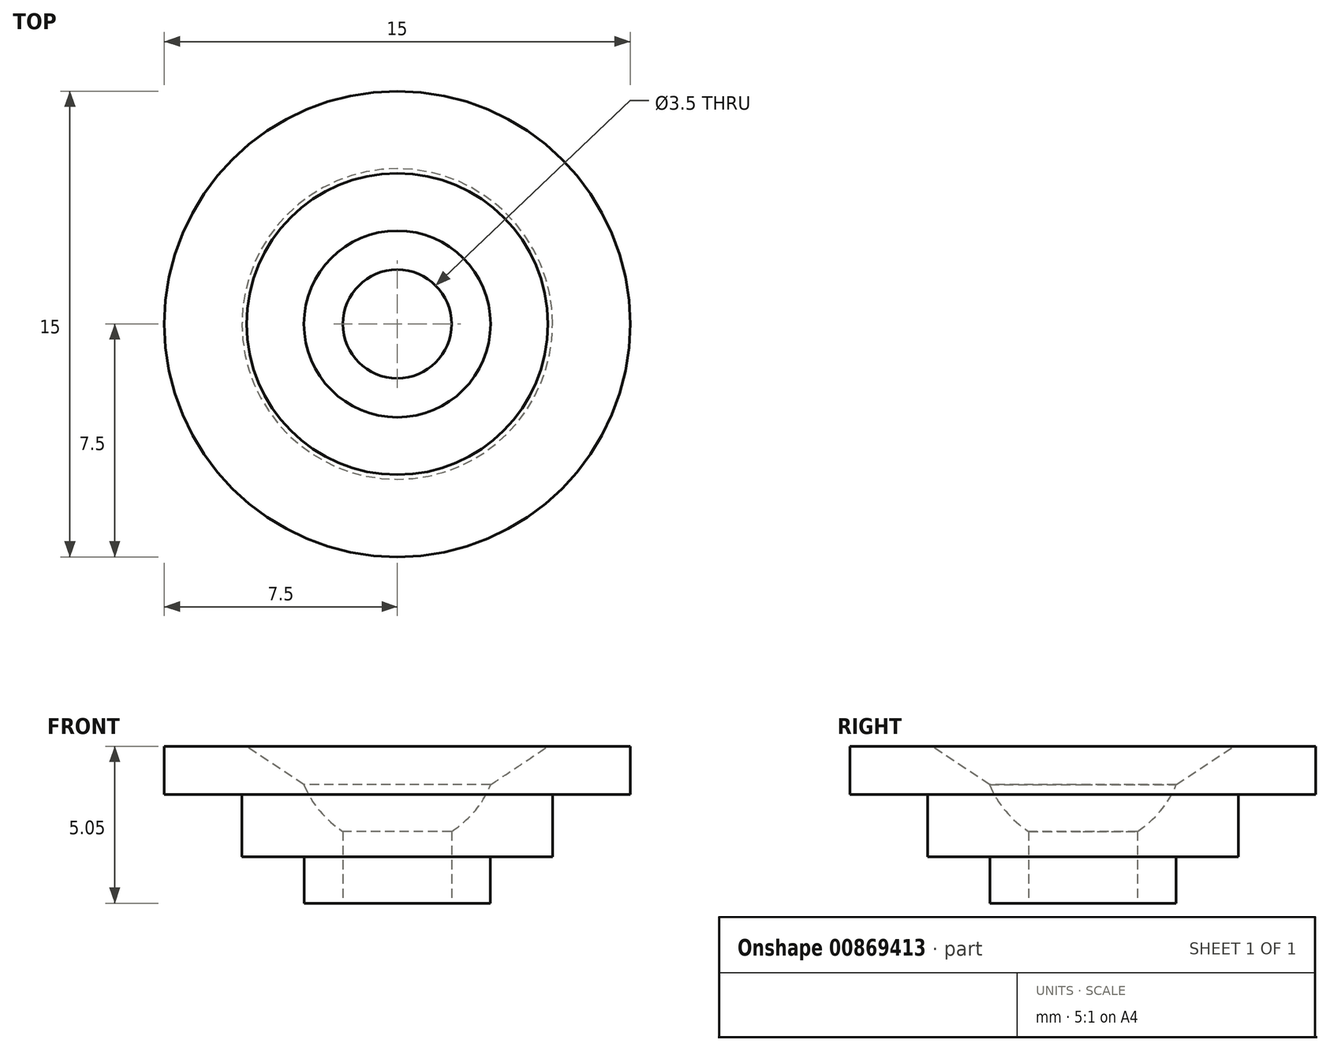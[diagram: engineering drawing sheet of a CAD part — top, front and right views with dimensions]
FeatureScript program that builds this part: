
annotation { "Feature Type Name" : "Feature", "Feature Type Description" : "" }
export const myFeature = defineFeature(function(context is Context, id is Id, definition is map)
    precondition{}
    {
        {
            var Q0;
            Q0=qCreatedBy(makeId("Top.planeOp"),FACE);
            var sketch = newSketch(context, id + "F0", { "sketchPlane" : qUnion([Q0])});
            skCircle(sketch, "E0", {"center": v(0, 0) * mm, "radius": 1.75 * mm});
            skCircle(sketch, "E1", {"center": v(0, 0) * mm, "radius": 7.5 * mm});
            skSolve(sketch);
        }
        {
            var Q0;
            Q0=makeQuery(id+"F0.imprint","IMPRINT",FACE,{"disambiguationData":[TD([[makeQuery(id+"F0.imprint","IMPRINT",EDGE,{"derivedFrom":sQuery(id+"F0.wireOp",EDGE,"E0")}),-1.0]])]});
            extrude(context, id + "F1", {"entities" : qUnion([Q0]), "depth" : 5.05 * mm, "offsetDistance" : 25 * mm});
        }
        {
            var Q0;
            Q0=qCreatedBy(makeId("Front.planeOp"),FACE);
            var sketch = newSketch(context, id + "F2", { "sketchPlane" : qUnion([Q0])});
            skLineSegment(sketch, "E2", {"start": v(0, 0) * mm, "end": v(0, 5.05) * mm, "construction": true});
            skLineSegment(sketch, "E3.0", {"start": v(-1.75, 5.05) * mm, "end": v(1.75, 5.05) * mm});
            skLineSegment(sketch, "E4", {"start": v(3, 0) * mm, "end": v(3, 1.5) * mm});
            skLineSegment(sketch, "E5", {"start": v(3, 1.5) * mm, "end": v(5, 1.5) * mm});
            skLineSegment(sketch, "E6", {"start": v(5, 1.5) * mm, "end": v(5, 3.5) * mm});
            skLineSegment(sketch, "E7", {"start": v(5, 3.5) * mm, "end": v(7.75, 3.5) * mm});
            skLineSegment(sketch, "E8", {"start": v(7.75, 3.5) * mm, "end": v(7.75, 0) * mm});
            skLineSegment(sketch, "E9", {"start": v(7.75, 0) * mm, "end": v(3, 0) * mm});
            skArc(sketch, "E10", {"start": v(0, 1.8) * mm, "mid": v(3.25, 5.05) * mm, "end": v(0, 8.3) * mm});
            skLineSegment(sketch, "E11", {"start": v(0, 1.8) * mm, "end": v(0, 8.3) * mm});
            skSolve(sketch);
        }
        {
            var Q0;
            Q0=makeQuery(id+"F2.imprint","IMPRINT",FACE,{"disambiguationData":[TD([[makeQuery(id+"F2.imprint","IMPRINT",EDGE,{"derivedFrom":sQuery(id+"F2.wireOp",EDGE,"E4")}),-1.0]])]});
            var Q1;
            Q1=makeQuery(id+"F2.imprint","IMPRINT",FACE,{"disambiguationData":[TD([[makeQuery(id+"F2.imprint","IMPRINT",EDGE,{"derivedFrom":sQuery(id+"F2.wireOp",EDGE,"E10")}),1.0]])]});
            var Q2;
            Q2=sQuery(id+"F2.wireOp",EDGE,"E2");
            revolve(context, id + "F3", {"operationType" : NewBodyOperationType.REMOVE, "surfaceOperationType" : NewSurfaceOperationType.NEW, "entities" : qUnion([Q0, Q1]), "axis" : qUnion([Q2]), "revolveType" : RevolveType.FULL, "oppositeDirection" : true});
        }
        {
            var Q0;
            Q0=makeQuery(id+"F3.boolean.opBoolean","INTERSECT",EDGE,{"derivedFrom":[makeQuery(id+"F1.opExtrude","CAP_FACE",FACE,{"disambiguationData":[OSD([sQuery(id+"F0.wireOp",EDGE,"E0"),sQuery(id+"F0.wireOp",EDGE,"E1")])],"isStart":false}),makeQuery(id+"F3.opRevolve","SWEPT_FACE",FACE,{"disambiguationData":[OSD([sQuery(id+"F2.wireOp",EDGE,"E10")])]})]});
            chamfer(context, id + "F4", {"entities" : qUnion([Q0]), "width" : 2 * mm, "tangentPropagation" : true});
        }
    });
